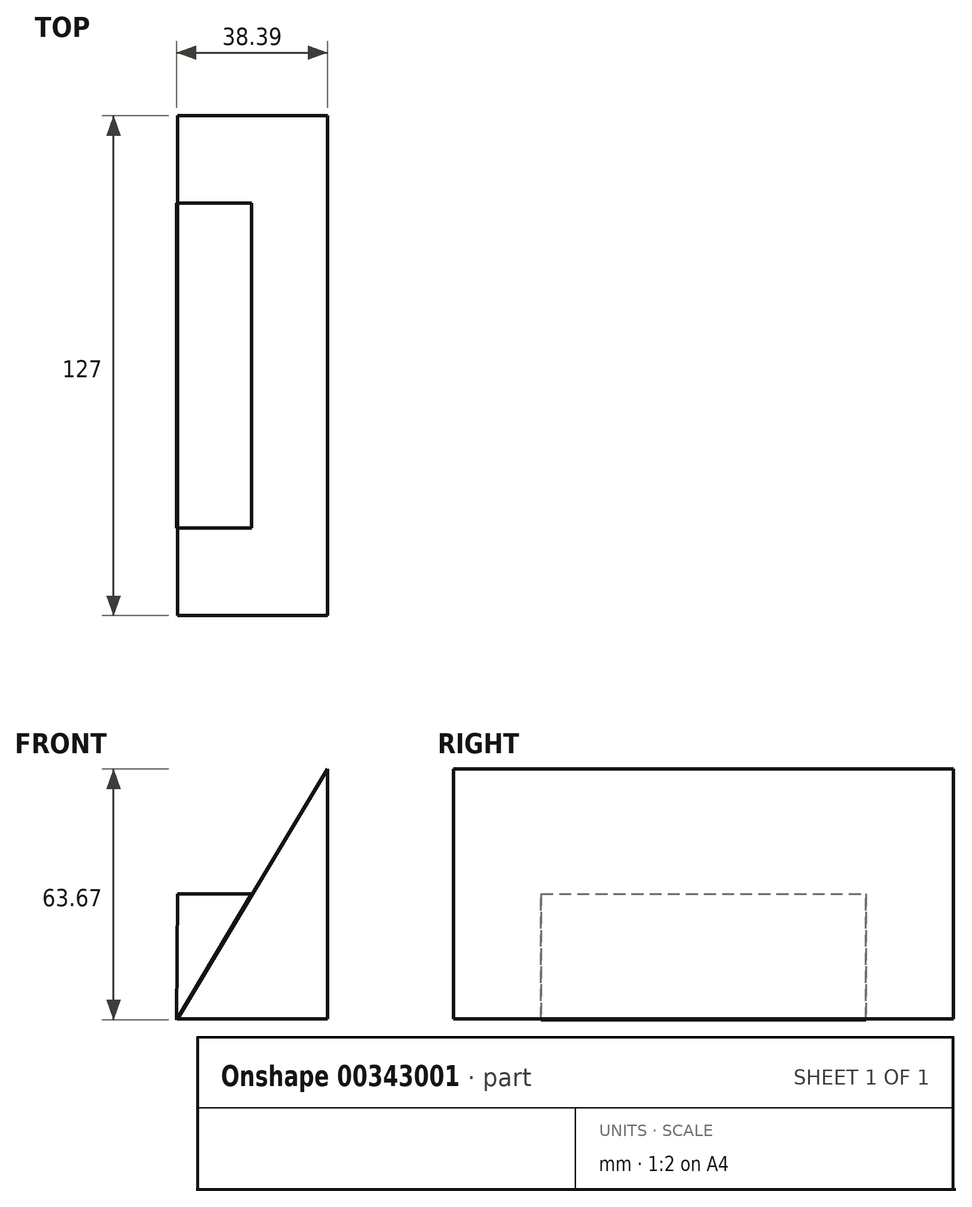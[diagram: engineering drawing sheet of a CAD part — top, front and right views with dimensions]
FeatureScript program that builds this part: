
annotation { "Feature Type Name" : "Feature", "Feature Type Description" : "" }
export const myFeature = defineFeature(function(context is Context, id is Id, definition is map)
    precondition{}
    {
        {
            var Q0;
            Q0=qCreatedBy(makeId("Front.planeOp"),FACE);
            var sketch = newSketch(context, id + "F0", { "sketchPlane" : qUnion([Q0])});
            skLineSegment(sketch, "E0", {"start": v(22.94, -31.75) * mm, "end": v(22.94, 31.75) * mm});
            skLineSegment(sketch, "E1", {"start": v(22.94, -31.75) * mm, "end": v(-15.16, -31.75) * mm});
            skLineSegment(sketch, "E2", {"start": v(-15.16, -31.75) * mm, "end": v(22.94, 31.75) * mm});
            skLineSegment(sketch, "E3", {"start": v(-15.16, -31.75) * mm, "end": v(-15.16, 0) * mm});
            skLineSegment(sketch, "E4", {"start": v(-15.16, 0) * mm, "end": v(3.9, 0) * mm});
            skLineSegment(sketch, "E5", {"start": v(22.94, 31.75) * mm, "end": v(-15.16, -31.75) * mm});
            skSolve(sketch);
        }
        {
            var Q0;
            {var subQ0=sQuery(id+"F0.wireOp",EDGE,"E0");Q0=makeQuery(id+"F0.imprint","IMPRINT",FACE,{"disambiguationData":[TD([[makeQuery(id+"F0.imprint","IMPRINT",EDGE,{"derivedFrom":subQ0}),1.0]])]});}
            extrude(context, id + "F1", {"entities" : qUnion([Q0]), "depth" : 127 * mm});
        }
        {
            var Q0;
            Q0=qCreatedBy(makeId("Front.planeOp"),FACE);
            var sketch = newSketch(context, id + "F2", { "sketchPlane" : qUnion([Q0])});
            skLineSegment(sketch, "E6", {"start": v(-15.45, -31.92) * mm, "end": v(22.74, 31.92) * mm});
            skLineSegment(sketch, "E7", {"start": v(22.74, 31.92) * mm, "end": v(3.64, 0) * mm});
            skLineSegment(sketch, "E8", {"start": v(3.64, 0) * mm, "end": v(-15.16, 0) * mm});
            skLineSegment(sketch, "E9", {"start": v(-15.16, 0) * mm, "end": v(-15.45, -31.92) * mm});
            skLineSegment(sketch, "E10", {"start": v(22.74, 31.92) * mm, "end": v(22.74, -31.92) * mm});
            skLineSegment(sketch, "E11", {"start": v(22.74, -31.92) * mm, "end": v(-15.45, -31.92) * mm});
            skSolve(sketch);
        }
        {
            var Q0;
            Q0=makeQuery(id+"F2.imprint","IMPRINT",FACE,{"disambiguationData":[TD([[makeQuery(id+"F2.imprint","IMPRINT",EDGE,{"derivedFrom":sQuery(id+"F2.wireOp",EDGE,"E6")}),1.0]])]});
            extrude(context, id + "F3", {"entities" : qUnion([Q0]), "depth" : 104.77 * mm, "hasSecondDirection" : true, "secondDirectionOppositeDirection" : false, "secondDirectionDepth" : 22.22 * mm});
        }
    });
